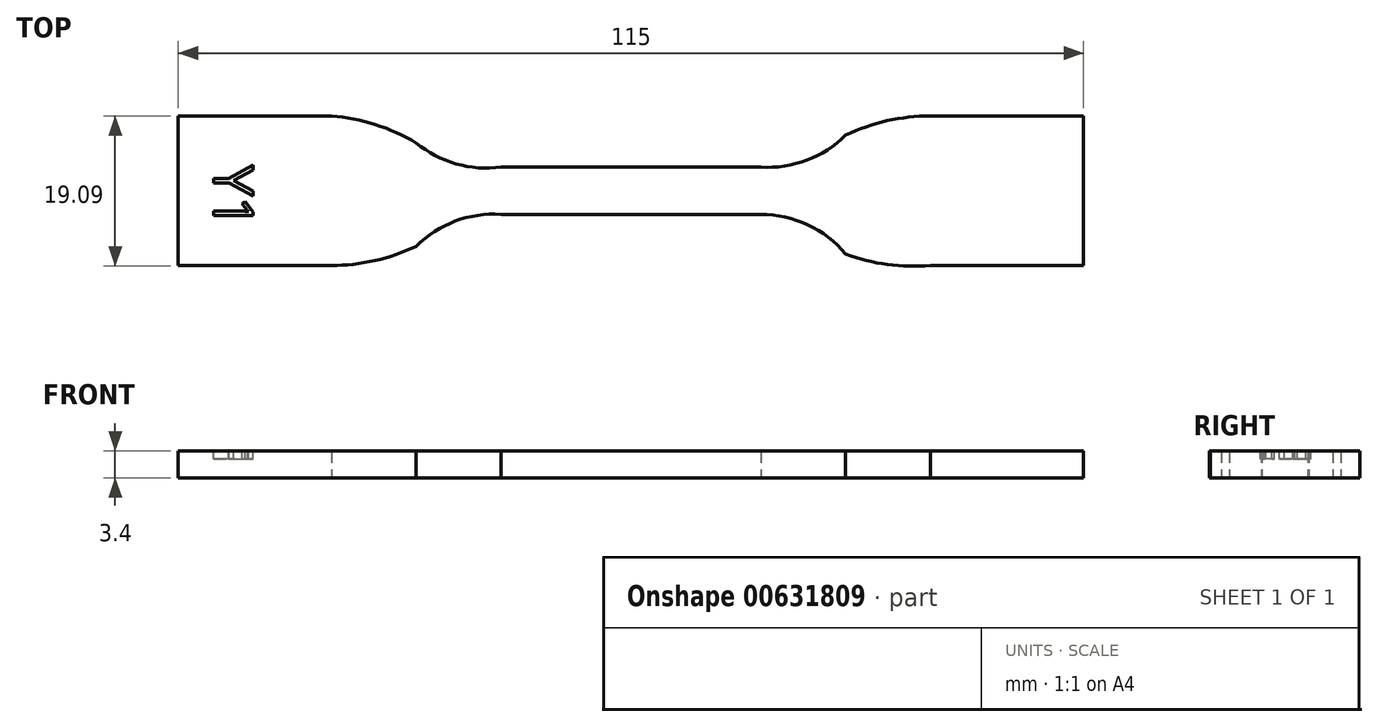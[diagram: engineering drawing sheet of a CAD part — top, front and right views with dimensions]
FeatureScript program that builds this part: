
annotation { "Feature Type Name" : "Feature", "Feature Type Description" : "" }
export const myFeature = defineFeature(function(context is Context, id is Id, definition is map)
    precondition{}
    {
        {
            var Q0;
            Q0=qCreatedBy(makeId("Top.planeOp"),FACE);
            var sketch = newSketch(context, id + "F0", { "sketchPlane" : qUnion([Q0])});
            skLineSegment(sketch, "E0", {"start": v(-33.87, 19.78) * mm, "end": v(-33.87, 0.78) * mm});
            skLineSegment(sketch, "E1", {"start": v(-33.87, 0.78) * mm, "end": v(-14.43, 0.78) * mm});
            skLineSegment(sketch, "E2", {"start": v(-33.87, 19.78) * mm, "end": v(-14.43, 19.78) * mm});
            skLineSegment(sketch, "E3", {"start": v(61.69, 19.78) * mm, "end": v(81.13, 19.78) * mm});
            skLineSegment(sketch, "E4", {"start": v(81.13, 19.78) * mm, "end": v(81.13, 0.78) * mm});
            skLineSegment(sketch, "E5", {"start": v(81.13, 0.78) * mm, "end": v(61.69, 0.78) * mm});
            skLineSegment(sketch, "E6", {"start": v(7.13, 13.28) * mm, "end": v(40.13, 13.28) * mm});
            skLineSegment(sketch, "E7", {"start": v(7.13, 7.28) * mm, "end": v(40.13, 7.28) * mm});
            skArc(sketch, "E8", {"start": v(-3.65, 16.36) * mm, "mid": v(-8.85, 18.69) * mm, "end": v(-14.43, 19.78) * mm});
            skArc(sketch, "E9", {"start": v(-3.65, 16.36) * mm, "mid": v(1.42, 13.7) * mm, "end": v(7.13, 13.28) * mm});
            skArc(sketch, "E10", {"start": v(-14.43, 0.78) * mm, "mid": v(-8.9, 1.4) * mm, "end": v(-3.65, 3.22) * mm});
            skArc(sketch, "E11", {"start": v(7.13, 7.28) * mm, "mid": v(1.3, 6.41) * mm, "end": v(-3.65, 3.22) * mm});
            skArc(sketch, "E12", {"start": v(40.13, 13.28) * mm, "mid": v(45.95, 14.15) * mm, "end": v(50.9, 17.34) * mm});
            skArc(sketch, "E13", {"start": v(61.69, 19.78) * mm, "mid": v(56.16, 19.16) * mm, "end": v(50.9, 17.34) * mm});
            skArc(sketch, "E14", {"start": v(50.9, 2.21) * mm, "mid": v(46.08, 5.95) * mm, "end": v(40.13, 7.28) * mm});
            skArc(sketch, "E15", {"start": v(50.9, 2.21) * mm, "mid": v(56.22, 0.9) * mm, "end": v(61.69, 0.78) * mm});
            skSolve(sketch);
        }
        {
            var Q0;
            Q0=qSketchRegion(id+"F0",true);
            extrude(context, id + "F1", {"entities" : qUnion([Q0]), "depth" : 3.4 * mm, "offsetDistance" : 25 * mm});
        }
        {
            var Q0;
            Q0=makeQuery(id+"F1.opExtrude","CAP_FACE",FACE,{"disambiguationData":[OSD([sQuery(id+"F0.wireOp",EDGE,"E0"),sQuery(id+"F0.wireOp",EDGE,"E1"),sQuery(id+"F0.wireOp",EDGE,"E2"),sQuery(id+"F0.wireOp",EDGE,"E3"),sQuery(id+"F0.wireOp",EDGE,"E4"),sQuery(id+"F0.wireOp",EDGE,"E5"),sQuery(id+"F0.wireOp",EDGE,"E6"),sQuery(id+"F0.wireOp",EDGE,"E7"),sQuery(id+"F0.wireOp",EDGE,"E8"),sQuery(id+"F0.wireOp",EDGE,"E9"),sQuery(id+"F0.wireOp",EDGE,"E10"),sQuery(id+"F0.wireOp",EDGE,"E11"),sQuery(id+"F0.wireOp",EDGE,"E12"),sQuery(id+"F0.wireOp",EDGE,"E13"),sQuery(id+"F0.wireOp",EDGE,"E14"),sQuery(id+"F0.wireOp",EDGE,"E15")])],"isStart":false});
            var sketch = newSketch(context, id + "F2", { "sketchPlane" : qUnion([Q0])});
            skText(sketch, "E16", { "text": "Y1", "fontName": "OpenSans-Regular.ttf"});
            const initialGuessF2  = {"E16": [-0.02939, 0.01353, 0, -1, 0.00508]};
            skSetInitialGuess(sketch, initialGuessF2);
            skSolve(sketch);
        }
        {
            var Q0;
            Q0 = qSketchRegion(id + "F2", true);
            extrude(context, id + "F3", {"entities" : qUnion([Q0]), "operationType" : NewBodyOperationType.REMOVE, "oppositeDirection" : true, "depth" : 1 * mm, "offsetDistance" : 25 * mm});
        }
    });
